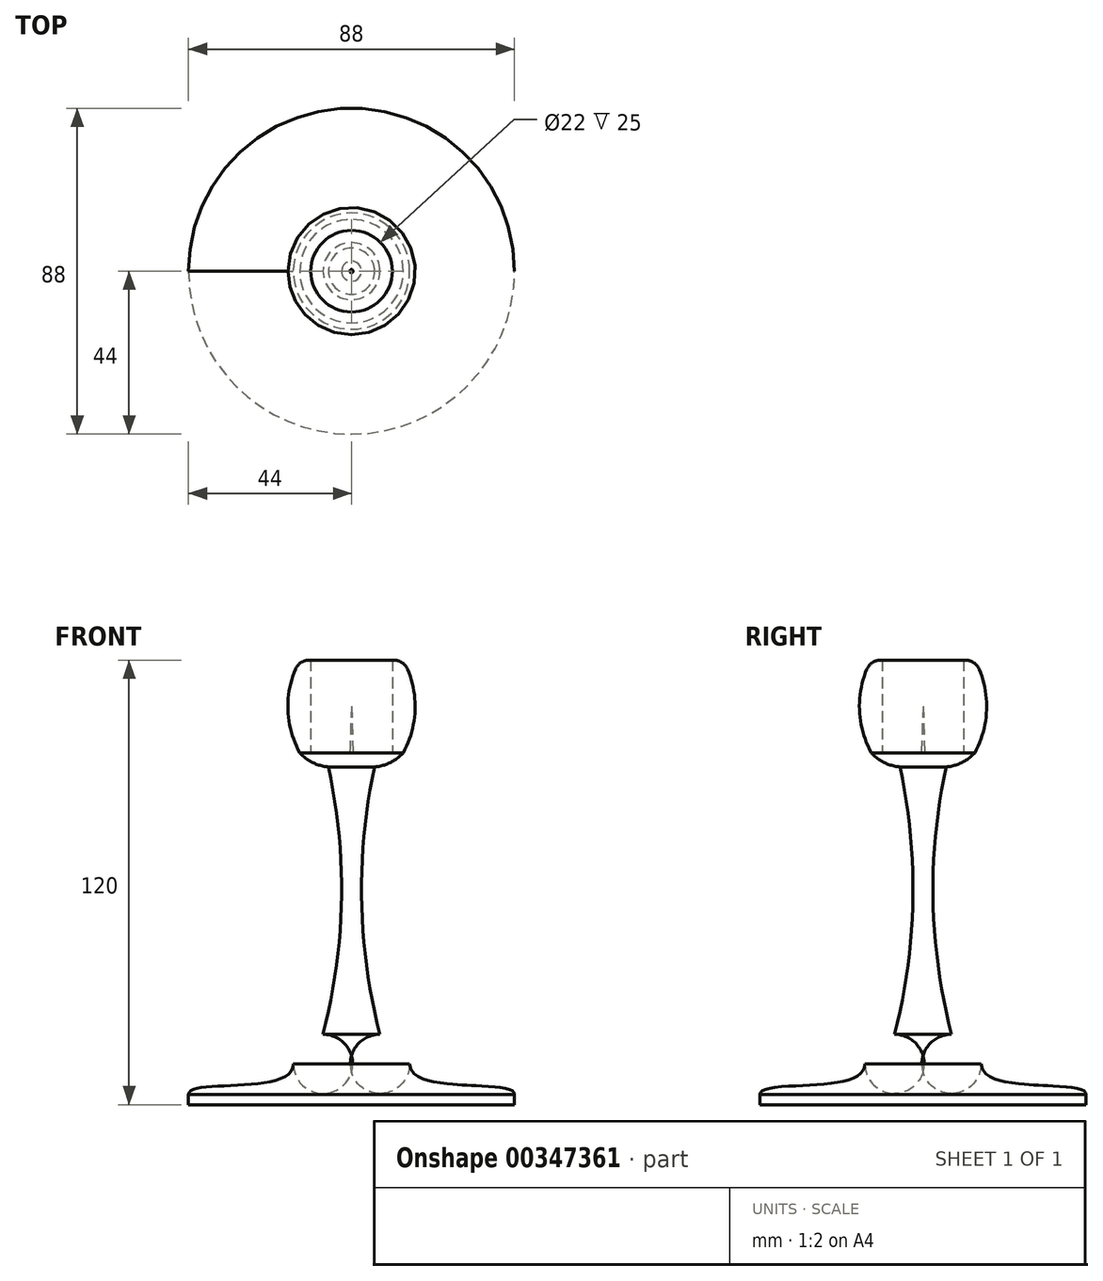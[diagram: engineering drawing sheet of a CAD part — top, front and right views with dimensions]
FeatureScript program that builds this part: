
annotation { "Feature Type Name" : "Feature", "Feature Type Description" : "" }
export const myFeature = defineFeature(function(context is Context, id is Id, definition is map)
    precondition{}
    {
        {
            assignVariable(context, id + "F0", {"name" : "D", "anyValue" : 22});
        }
        {
            var Q0;
            Q0=qCreatedBy(makeId("Top.planeOp"),FACE);
            cPlane(context, id + "F1", {"entities" : qUnion([Q0]), "cplaneType" : CPlaneType.OFFSET, "offset" : (getVariable(context, 'D') / 2) * mm, "width" : 150 * mm, "height" : 150 * mm});
        }
        {
            var Q0;
            Q0=qCreatedBy(makeId("Top.planeOp"),FACE);
            var sketch = newSketch(context, id + "F2", { "sketchPlane" : qUnion([Q0])});
            skCircle(sketch, "E0", {"center": v(0, 0) * mm, "radius": 11 * mm});
            skCircle(sketch, "E1", {"center": v(0, 0) * mm, "radius": 13.75 * mm});
            skCircle(sketch, "E2", {"center": v(0, 0) * mm, "radius": 44 * mm});
            skSolve(sketch);
        }
        {
            var Q0;
            Q0=makeQuery(id+"F2.imprint","IMPRINT",FACE,{"disambiguationData":[TD([[makeQuery(id+"F2.imprint","IMPRINT",EDGE,{"derivedFrom":sQuery(id+"F2.wireOp",EDGE,"E1")}),-1.0]])]});
            var Q1;
            Q1=makeQuery(id+"F2.imprint","IMPRINT",FACE,{"disambiguationData":[TD([[makeQuery(id+"F2.imprint","IMPRINT",EDGE,{"derivedFrom":sQuery(id+"F2.wireOp",EDGE,"E0")}),-1.0]])]});
            var Q2;
            Q2=makeQuery(id+"F2.imprint","IMPRINT",FACE,{"disambiguationData":[TD([[makeQuery(id+"F2.imprint","IMPRINT",EDGE,{"derivedFrom":sQuery(id+"F2.wireOp",EDGE,"E0")}),1.0]])]});
            extrude(context, id + "F3", {"entities" : qUnion([Q0, Q1, Q2]), "depth" : (getVariable(context, 'D') / 8) * mm});
        }
        {
            var Q0;
            Q0=qCreatedBy(id+"F1.planeOp",FACE);
            var sketch = newSketch(context, id + "F4", { "sketchPlane" : qUnion([Q0])});
            skCircle(sketch, "E3.0", {"center": v(0, 0) * mm, "radius": 15.68 * mm});
            skSolve(sketch);
        }
        {
            var Q1;
            Q1=makeQuery(id+"F3.opExtrude","CAP_FACE",FACE,{"disambiguationData":[OSD([sQuery(id+"F2.wireOp",EDGE,"E2")])],"isStart":false});
            var Q2;
            Q2 = qSketchRegion(id + "F4", true);
            loft(context, id + "F5", {"operationType" : NewBodyOperationType.ADD, "startCondition" : LoftEndDerivativeType.NORMAL_TO_PROFILE, "startMagnitude" : 1.3, "endCondition" : LoftEndDerivativeType.NORMAL_TO_PROFILE, "endMagnitude" : 2.5, "sheetProfilesArray" : [{ "sheetProfileEntities" : qUnion([Q1]) }, { "sheetProfileEntities" : qUnion([Q2]) }]});
        }
        {
            var Q0;
            Q0=qCreatedBy(makeId("Front.planeOp"),FACE);
            var sketch = newSketch(context, id + "F6", { "sketchPlane" : qUnion([Q0])});
            skLineSegment(sketch, "E4", {"start": v(0, 0) * mm, "end": v(0, 95) * mm});
            skLineSegment(sketch, "E5", {"start": v(0.45, 95) * mm, "end": v(11, 95) * mm});
            skLineSegment(sketch, "E6", {"start": v(11, 95) * mm, "end": v(11, 120) * mm});
            skLineSegment(sketch, "E7", {"start": v(11, 120) * mm, "end": v(11.46, 120) * mm});
            skArc(sketch, "E8", {"start": v(13.96, 95) * mm, "mid": v(17.14, 106.14) * mm, "end": v(15.15, 117.55) * mm});
            skFitSpline(sketch, "E9.0", {"points": [v(15.68, 11) * mm, v(5.23, 11) * mm, v(-5.23, 11) * mm, v(-15.68, 11) * mm]});
            skArc(sketch, "E10", {"start": v(15.68, 11) * mm, "mid": v(13.34, 16.66) * mm, "end": v(7.68, 19) * mm});
            skArc(sketch, "E11", {"start": v(6.22, 91.18) * mm, "mid": v(2.72, 55) * mm, "end": v(7.68, 19) * mm});
            skPoint(sketch, "E11.startSnap0", {"position": v(6.22, 18.86) * mm});
            skArc(sketch, "E12", {"start": v(6.22, 91.18) * mm, "mid": v(10.46, 92.34) * mm, "end": v(13.96, 95) * mm});
            skPoint(sketch, "E13.visualSharp", {"position": v(13.96, 120) * mm});
            skArc(sketch, "E13.filletArc", {"start": v(15.15, 117.55) * mm, "mid": v(13.67, 119.33) * mm, "end": v(11.46, 120) * mm});
            skLineSegment(sketch, "E14", {"start": v(7.68, 19) * mm, "end": v(7.68, 11) * mm, "construction": true});
            skLineSegment(sketch, "E15", {"start": v(7.68, 11) * mm, "end": v(15.68, 11) * mm, "construction": true});
            skLineSegment(sketch, "E16", {"start": v(0.45, 95) * mm, "end": v(0, 107.5) * mm});
            skLineSegment(sketch, "E17", {"start": v(0, 107.5) * mm, "end": v(0, 95) * mm});
            skSolve(sketch);
        }
        {
            var Q0;
            {var subQ0=sQuery(id+"F6.wireOp",EDGE,"E5");Q0=makeQuery(id+"F6.imprint","IMPRINT",FACE,{"disambiguationData":[TD([[makeQuery(id+"F6.imprint","IMPRINT",EDGE,{"derivedFrom":subQ0}),-1.0]])]});}
            var Q1;
            Q1=sQuery(id+"F6.wireOp",EDGE,"E4");
            revolve(context, id + "F7", {"operationType" : NewBodyOperationType.ADD, "entities" : qUnion([Q0]), "axis" : qUnion([Q1]), "revolveType" : RevolveType.FULL});
        }
    });
